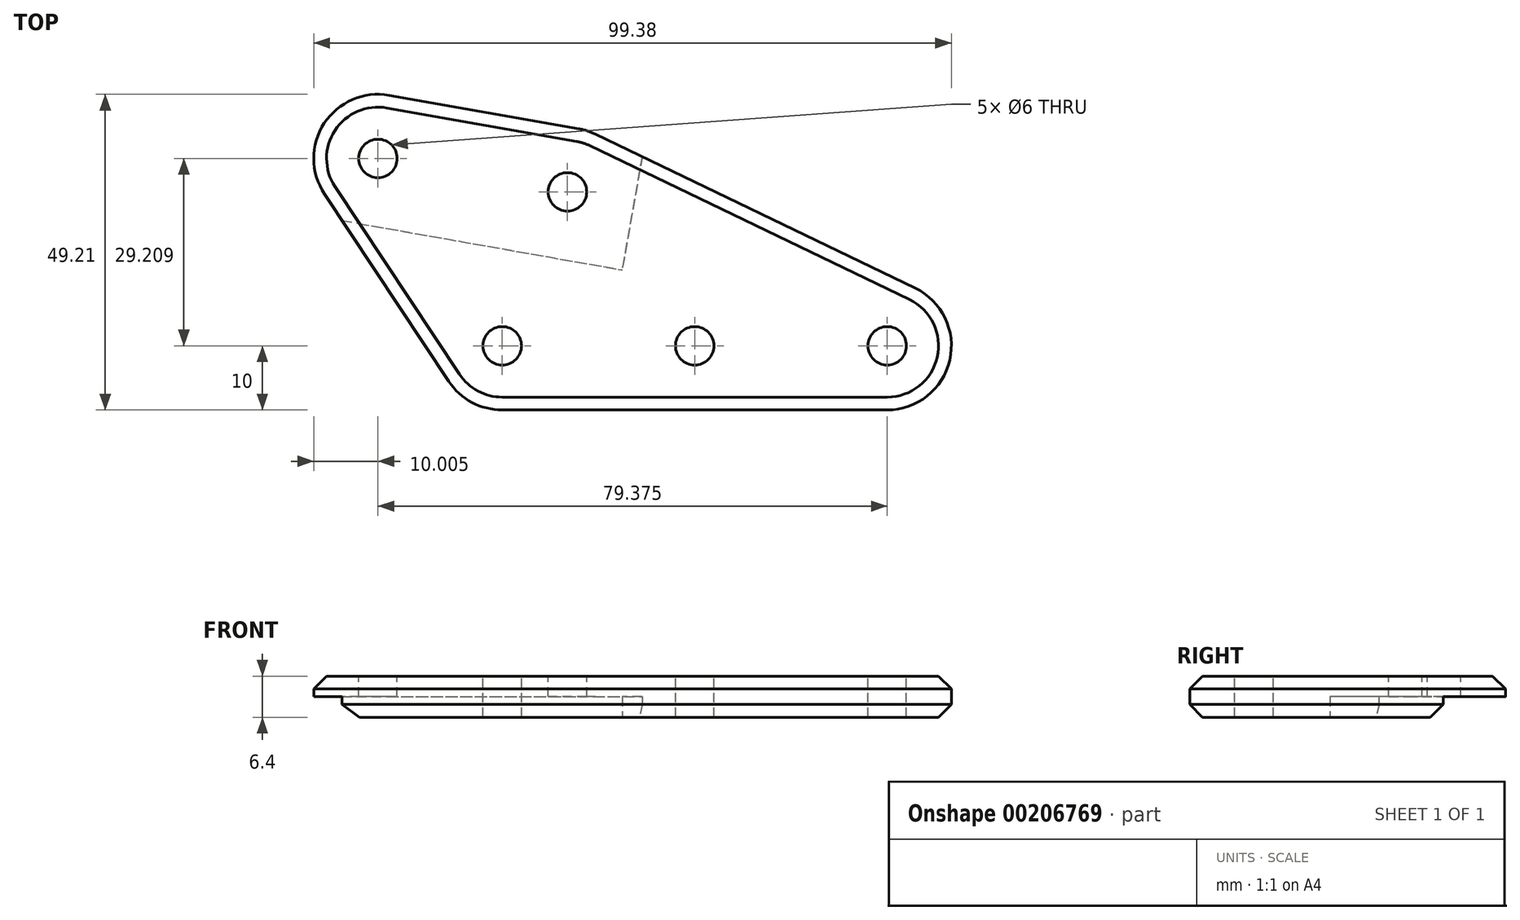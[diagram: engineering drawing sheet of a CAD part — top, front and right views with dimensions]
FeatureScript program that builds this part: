
annotation { "Feature Type Name" : "Feature", "Feature Type Description" : "" }
export const myFeature = defineFeature(function(context is Context, id is Id, definition is map)
    precondition{}
    {
        {
            var Q0;
            Q0=qCreatedBy(makeId("Top.planeOp"),FACE);
            var sketch = newSketch(context, id + "F0", { "sketchPlane" : qUnion([Q0])});
            skLineSegment(sketch, "E0", {"start": v(-30, -10) * mm, "end": v(-90, -10) * mm});
            skCircle(sketch, "E1", {"center": v(-90, 0) * mm, "radius": 3 * mm});
            skCircle(sketch, "E2", {"center": v(-109.38, 29.2) * mm, "radius": 3 * mm});
            skCircle(sketch, "E3", {"center": v(-79.83, 24) * mm, "radius": 3 * mm});
            skLineSegment(sketch, "E4", {"start": v(-90, 0) * mm, "end": v(-60, 0) * mm});
            skLineSegment(sketch, "E5", {"start": v(-30, 0) * mm, "end": v(0, 0) * mm});
            skLineSegment(sketch, "E6", {"start": v(-60, 0) * mm, "end": v(-30, 0) * mm});
            skLineSegment(sketch, "E7", {"start": v(-109.38, 29.2) * mm, "end": v(-79.83, 24) * mm});
            skCircle(sketch, "E8", {"center": v(-109.38, 29.2) * mm, "radius": 10 * mm});
            skCircle(sketch, "E9", {"center": v(-90, 0) * mm, "radius": 10 * mm});
            skCircle(sketch, "E10", {"center": v(-79.83, 24) * mm, "radius": 10 * mm});
            skLineSegment(sketch, "E11", {"start": v(-107.64, 39.06) * mm, "end": v(-78.1, 33.85) * mm});
            skPoint(sketch, "E12.startSnap0", {"position": v(-45, 0) * mm});
            skPoint(sketch, "E13.newPointB", {"position": v(1.6, -3374380.4) * mm});
            skLineSegment(sketch, "E14", {"start": v(-75.5, 33) * mm, "end": v(-25.66, 9) * mm});
            skLineSegment(sketch, "E15", {"start": v(-79.83, 24) * mm, "end": v(56.28, 0) * mm});
            skLineSegment(sketch, "E16", {"start": v(0, 0) * mm, "end": v(56.28, 0) * mm});
            skCircle(sketch, "E17", {"center": v(-60, 0) * mm, "radius": 3 * mm});
            skCircle(sketch, "E18", {"center": v(-30, 0) * mm, "radius": 3 * mm});
            skCircle(sketch, "E19", {"center": v(-30, 0) * mm, "radius": 10 * mm});
            skLineSegment(sketch, "E20", {"start": v(-117.7, 23.68) * mm, "end": v(-98.33, -5.53) * mm});
            skLineSegment(sketch, "E21.bottom", {"start": v(-102, 0) * mm, "end": v(-134.42, 0) * mm});
            skLineSegment(sketch, "E21.top", {"start": v(-102, -10) * mm, "end": v(-134.42, -10) * mm});
            skLineSegment(sketch, "E21.left", {"start": v(-102, 0) * mm, "end": v(-102, -10) * mm});
            skLineSegment(sketch, "E21.right", {"start": v(-134.42, 0) * mm, "end": v(-134.42, -10) * mm});
            skSolve(sketch);
        }
        {
            var Q0;
            {var subQ0=sQuery(id+"F0.wireOp",EDGE,"E14");var subQ1=sQuery(id+"F0.wireOp",EDGE,"E10");var subQ2=makeQuery(id+"F0.imprint","INTERSECT",VERTEX,{"derivedFrom":[subQ1,subQ0]});Q0=makeQuery(id+"F0.imprint","IMPRINT",FACE,{"disambiguationData":[TD([[makeQuery(id+"F0.imprint","IMPRINT",EDGE,{"disambiguationData":[TD([[subQ2,1.0]])],"derivedFrom":subQ1}),-1.0]])]});}
            var Q1;
            {var subQ6=sQuery(id+"F0.wireOp",EDGE,"E0");Q1=makeQuery(id+"F0.imprint","IMPRINT",FACE,{"disambiguationData":[TD([[makeQuery(id+"F0.imprint","IMPRINT",EDGE,{"derivedFrom":subQ6}),-1.0]])]});}
            var Q2;
            {var subQ5=sQuery(id+"F0.wireOp",EDGE,"E11");Q2=makeQuery(id+"F0.imprint","IMPRINT",FACE,{"disambiguationData":[TD([[makeQuery(id+"F0.imprint","IMPRINT",EDGE,{"derivedFrom":subQ5}),-1.0]])]});}
            var Q3;
            {var subQ5=sQuery(id+"F0.wireOp",EDGE,"E11");Q3=makeQuery(id+"F0.imprint","IMPRINT",FACE,{"disambiguationData":[TD([[makeQuery(id+"F0.imprint","IMPRINT",EDGE,{"derivedFrom":subQ5}),-1.0]])]});}
            var Q4;
            {var subQ0=sQuery(id+"F0.wireOp",EDGE,"E7");var subQ1=sQuery(id+"F0.wireOp",EDGE,"E3");var subQ2=makeQuery(id+"F0.imprint","INTERSECT",VERTEX,{"derivedFrom":[subQ1,subQ0]});Q4=makeQuery(id+"F0.imprint","IMPRINT",FACE,{"disambiguationData":[TD([[makeQuery(id+"F0.imprint","IMPRINT",EDGE,{"disambiguationData":[TD([[subQ2,-1.0]])],"derivedFrom":subQ1}),-1.0]])]});}
            var Q5;
            {var subQ0=sQuery(id+"F0.wireOp",EDGE,"E14");var subQ1=sQuery(id+"F0.wireOp",EDGE,"E10");var subQ2=makeQuery(id+"F0.imprint","INTERSECT",VERTEX,{"derivedFrom":[subQ1,subQ0]});Q5=makeQuery(id+"F0.imprint","IMPRINT",FACE,{"disambiguationData":[TD([[makeQuery(id+"F0.imprint","IMPRINT",EDGE,{"disambiguationData":[TD([[subQ2,1.0]])],"derivedFrom":subQ1}),-1.0]])]});}
            var Q6;
            {var subQ2=sQuery(id+"F0.wireOp",EDGE,"E7");var subQ5=sQuery(id+"F0.wireOp",EDGE,"E3");var subQ9=makeQuery(id+"F0.imprint","INTERSECT",VERTEX,{"derivedFrom":[subQ5,subQ2]});Q6=makeQuery(id+"F0.imprint","IMPRINT",FACE,{"disambiguationData":[TD([[makeQuery(id+"F0.imprint","IMPRINT",EDGE,{"disambiguationData":[TD([[subQ9,1.0]])],"derivedFrom":subQ5}),-1.0]])]});}
            var Q7;
            {var subQ1=sQuery(id+"F0.wireOp",EDGE,"E4");var subQ16=sQuery(id+"F0.wireOp",EDGE,"E9");var subQ18=makeQuery(id+"F0.imprint","INTERSECT",VERTEX,{"derivedFrom":[subQ1,subQ16]});Q7=makeQuery(id+"F0.imprint","IMPRINT",FACE,{"disambiguationData":[TD([[makeQuery(id+"F0.imprint","IMPRINT",EDGE,{"disambiguationData":[TD([[subQ18,-1.0]])],"derivedFrom":subQ1}),1.0]])]});}
            var Q8;
            {var subQ6=sQuery(id+"F0.wireOp",EDGE,"E0");Q8=makeQuery(id+"F0.imprint","IMPRINT",FACE,{"disambiguationData":[TD([[makeQuery(id+"F0.imprint","IMPRINT",EDGE,{"derivedFrom":subQ6}),-1.0]])]});}
            var Q9;
            Q9=makeQuery(id+"F0.imprint","IMPRINT",FACE,{"disambiguationData":[TD([[makeQuery(id+"F0.imprint","IMPRINT",EDGE,{"derivedFrom":sQuery(id+"F0.wireOp",EDGE,"E1")}),-1.0]])]});
            var Q10;
            Q10=makeQuery(id+"F0.imprint","IMPRINT",FACE,{"disambiguationData":[TD([[makeQuery(id+"F0.imprint","IMPRINT",EDGE,{"derivedFrom":sQuery(id+"F0.wireOp",EDGE,"E2")}),-1.0]])]});
            var Q11;
            {var subQ1=sQuery(id+"F0.wireOp",EDGE,"E5");var subQ5=sQuery(id+"F0.wireOp",EDGE,"E19");var subQ8=makeQuery(id+"F0.imprint","INTERSECT",VERTEX,{"derivedFrom":[subQ1,subQ5]});Q11=makeQuery(id+"F0.imprint","IMPRINT",FACE,{"disambiguationData":[TD([[makeQuery(id+"F0.imprint","IMPRINT",EDGE,{"disambiguationData":[TD([[subQ8,1.0]])],"derivedFrom":subQ1}),-1.0]])]});}
            var Q12;
            {var subQ0=sQuery(id+"F0.wireOp",EDGE,"E19");var subQ2=sQuery(id+"F0.wireOp",EDGE,"E5");var subQ3=makeQuery(id+"F0.imprint","INTERSECT",VERTEX,{"derivedFrom":[subQ2,subQ0]});Q12=makeQuery(id+"F0.imprint","IMPRINT",FACE,{"disambiguationData":[TD([[makeQuery(id+"F0.imprint","IMPRINT",EDGE,{"disambiguationData":[TD([[subQ3,1.0]])],"derivedFrom":subQ2}),1.0]])]});}
            extrude(context, id + "F1", {"entities" : qUnion([Q0, Q1, Q2, Q3, Q4, Q5, Q6, Q7, Q8, Q9, Q10, Q11, Q12]), "depth" : 6.4 * mm});
        }
        {
            var Q0;
            Q0=makeQuery(id+"F1.opExtrude","CAP_FACE",FACE,{"disambiguationData":[OSD([sQuery(id+"F0.wireOp",EDGE,"E0"),sQuery(id+"F0.wireOp",EDGE,"6dyDcM5c-1yAg-quQ1-icmL-2Ec9erfbZDdK"),sQuery(id+"F0.wireOp",EDGE,"E1"),sQuery(id+"F0.wireOp",EDGE,"E2"),sQuery(id+"F0.wireOp",EDGE,"E3"),sQuery(id+"F0.wireOp",EDGE,"E8"),sQuery(id+"F0.wireOp",EDGE,"E9"),sQuery(id+"F0.wireOp",EDGE,"MG3xochi-pTH6-NXDe-IZer-cky7eGSUGF28"),sQuery(id+"F0.wireOp",EDGE,"E10"),sQuery(id+"F0.wireOp",EDGE,"4jy32K5d-2140-3yTE-HOG5-iwpzrp11MGxu"),sQuery(id+"F0.wireOp",EDGE,"E11"),sQuery(id+"F0.wireOp",EDGE,"E14"),sQuery(id+"F0.wireOp",EDGE,"KXRvfklZ-nFMY-xIWL-Wxfe-Wy6mN7gEAxao"),sQuery(id+"F0.wireOp",EDGE,"E17"),sQuery(id+"F0.wireOp",EDGE,"E18")])],"isStart":false});
            cPlane(context, id + "F2", {"entities" : qUnion([Q0]), "cplaneType" : CPlaneType.OFFSET, "offset" : 0 * mm, "width" : 150 * mm, "height" : 150 * mm});
        }
        {
            var Q0;
            Q0=qCreatedBy(id+"F2.planeOp",FACE);
            var sketch = newSketch(context, id + "F3", { "sketchPlane" : qUnion([Q0])});
            skLineSegment(sketch, "E22", {"start": v(-125.64, 21.41) * mm, "end": v(-71.31, 11.84) * mm});
            skCircle(sketch, "E23", {"center": v(-109.38, 29.2) * mm, "radius": 10.5 * mm});
            skCircle(sketch, "E24", {"center": v(-79.83, 24) * mm, "radius": 10.5 * mm});
            skLineSegment(sketch, "E25", {"start": v(-125.64, 21.41) * mm, "end": v(-121.52, 44.76) * mm});
            skLineSegment(sketch, "E26", {"start": v(-121.52, 44.76) * mm, "end": v(-67.2, 35.18) * mm});
            skLineSegment(sketch, "E27", {"start": v(-67.2, 35.18) * mm, "end": v(-71.31, 11.84) * mm});
            skSolve(sketch);
        }
        {
            var Q0;
            Q0=qSketchRegion(id+"F3",true);
            extrude(context, id + "F4", {"entities" : qUnion([Q0]), "operationType" : NewBodyOperationType.REMOVE, "oppositeDirection" : true, "depth" : 3.2 * mm});
        }
        {
            var Q0;
            Q0=makeQuery(id+"F1.opExtrude","CAP_EDGE",EDGE,{"disambiguationData":[OSD([sQuery(id+"F0.wireOp",EDGE,"E14")])],"isStart":true});
            var Q1;
            Q1=makeQuery(id+"F1.opExtrude","CAP_EDGE",EDGE,{"disambiguationData":[OSD([sQuery(id+"F0.wireOp",EDGE,"E14")])],"isStart":false});
            chamfer(context, id + "F5", {"entities" : qUnion([Q0, Q1]), "width" : 2 * mm, "tangentPropagation" : true});
        }
        {
            var Q0;
            Q0=makeQuery(id+"F1.opExtrude","SWEPT_BODY",BODY,{"disambiguationData":[OSD([sQuery(id+"F0.wireOp",EDGE,"E0"),sQuery(id+"F0.wireOp",EDGE,"E1"),sQuery(id+"F0.wireOp",EDGE,"E2"),sQuery(id+"F0.wireOp",EDGE,"E3"),sQuery(id+"F0.wireOp",EDGE,"E8"),sQuery(id+"F0.wireOp",EDGE,"E9"),sQuery(id+"F0.wireOp",EDGE,"E10"),sQuery(id+"F0.wireOp",EDGE,"E11"),sQuery(id+"F0.wireOp",EDGE,"E14"),sQuery(id+"F0.wireOp",EDGE,"E17"),sQuery(id+"F0.wireOp",EDGE,"E18"),sQuery(id+"F0.wireOp",EDGE,"E19"),sQuery(id+"F0.wireOp",EDGE,"E20")])]});
            var Q1;
            Q1=makeQuery(id+"F1.opExtrude","CAP_FACE",FACE,{"disambiguationData":[OSD([sQuery(id+"F0.wireOp",EDGE,"E0"),sQuery(id+"F0.wireOp",EDGE,"E1"),sQuery(id+"F0.wireOp",EDGE,"E2"),sQuery(id+"F0.wireOp",EDGE,"E3"),sQuery(id+"F0.wireOp",EDGE,"E8"),sQuery(id+"F0.wireOp",EDGE,"E9"),sQuery(id+"F0.wireOp",EDGE,"E10"),sQuery(id+"F0.wireOp",EDGE,"E11"),sQuery(id+"F0.wireOp",EDGE,"E14"),sQuery(id+"F0.wireOp",EDGE,"E17"),sQuery(id+"F0.wireOp",EDGE,"E18"),sQuery(id+"F0.wireOp",EDGE,"E19"),sQuery(id+"F0.wireOp",EDGE,"E20")])],"isStart":false});
            mirror(context, id + "F6", {"entities" : qUnion([Q0]), "mirrorPlane" : qUnion([Q1])});
        }
        {
            var Q0;
            Q0=makeQuery(id+"F1.opExtrude","SWEPT_BODY",BODY,{"disambiguationData":[OSD([sQuery(id+"F0.wireOp",EDGE,"E0"),sQuery(id+"F0.wireOp",EDGE,"E1"),sQuery(id+"F0.wireOp",EDGE,"E2"),sQuery(id+"F0.wireOp",EDGE,"E3"),sQuery(id+"F0.wireOp",EDGE,"E8"),sQuery(id+"F0.wireOp",EDGE,"E9"),sQuery(id+"F0.wireOp",EDGE,"E10"),sQuery(id+"F0.wireOp",EDGE,"E11"),sQuery(id+"F0.wireOp",EDGE,"E14"),sQuery(id+"F0.wireOp",EDGE,"E17"),sQuery(id+"F0.wireOp",EDGE,"E18"),sQuery(id+"F0.wireOp",EDGE,"E19"),sQuery(id+"F0.wireOp",EDGE,"E20")])]});
            deleteBodies(context, id + "F7", {"entities" : qUnion([Q0])});
        }
    });
